# Revit family: LAMP_FLUT G2 ASYMMETRIC
name_source: partatom
category: Modelos genéricos
revit_build: Autodesk Revit 2015 (Build: 20140606_1530(x64)
units: mm (PartAtom-declared; Revit-internal decimal feet)

## types (12) — shared parameters
CRI = 70
Dimensions = 530 x 280 x 60
Elevación por defecto = 1219 mm
Fabricante = LAMP
Gear = Electronic
Installation instructions = https://www.lamp.es
Insulation class = I
Lamp = HIGH POWER LED
Last update = 22/08/2019
Luminaire type = OUTDOOR - FLOODLIGHT
MacAdam = 4
Manufacturer URL = http://www.lamp.es
Manufacturer country = Spain
Manufacturer name = LAMP
Material Rótula = LAMP_Acero inoxidable AISI 304
Material cuerpo = LAMP_Aluminio Cuerpo Flut ANT
Model explanation = Availability of tilting between 0º and -30º (or 120º) when placed in a project.
Power Supply = 220-240V 50-60Hz
Product URL = https://www.lamp.es
Product datasheet = http://www.lamp.es
Protection rating = IP66 / IK06
Type = HIGH POWER PHILIPS

## per-type parameters (varying)
| type | Descripción | Efficacy | Finish | IEE | Initial color | Initial intensity | LED Lifetime | Modelo | Photometric web file | Plum | Power | Product code | Weight |
| 7329LM 3000 ANTHRACITE | FLUT G2 9300 WW ASYM ANT. | 114 lm/W | Textured anthracite grey | A+ | 3000 K | 7329 lm | 50.000 L90 B10 | FL209AS730NA | Cuerpo Flut G2 - Asym : 7329LM 3000 ANTHRACITE | 64 W | 59 W | FL209AS730NA | 7.86 kg |
| 7329LM 3000 GREY | FLUT G2 9300 WW ASYM GR. | 114 lm/W | Texturised grey | A+ | 3000 K | 7329 lm | 50.000 L90 B10 | FL209AS730NG | Cuerpo Flut G2 - Asym : 7329LM 3000 GREY | 64 W | 59 W | FL209AS730NG | 7.86 kg |
| 7715LM 4000 ANTHRACITE | FLUT G2 9300 NW ASYM ANT. | 120 lm/W | Textured anthracite grey | A++ | 4000 K | 7715 lm | 50.000 L90 B10 | FL209AS740NA | Cuerpo Flut G2 - Asym : 7715LM 4000 ANTHRACITE | 64 W | 59 W | FL209AS740NA | 7.86 kg |
| 7715LM 4000 GREY | FLUT G2 9300 NW ASYM GR. | 120 lm/W | Texturised grey | A++ | 4000 K | 7715 lm | 50.000 L90 B10 | FL209AS740NG | Cuerpo Flut G2 - Asym : 7715LM 4000 GREY | 64 W | 59 W | FL209AS740NG | 7.86 kg |
| 11068LM 3000 ANTHRACITE | FLUT G2 14000 WW ASYM ANT. | 114 lm/W | Textured anthracite grey | A+ | 3000 K | 11068 lm | 80.000 L80 B10 | FL214AS730NA | Cuerpo Flut G2 - Asym : 11068LM 3000 ANTHRACITE | 97 W | 88 W | FL214AS730NA | 7.94 kg |
| 11068LM 3000 GREY | FLUT G2 14000 WW ASYM GR. | 114 lm/W | Texturised grey | A+ | 3000 K | 11068 lm | 80.000 L80 B10 | FL214AS730NG | Cuerpo Flut G2 - Asym : 11068LM 3000 GREY | 97 W | 88 W | FL214AS730NG | 7.94 kg |
| 11650LM 4000 ANTHRACITE | FLUT G2 14000 NW ASYM ANT. | 120 lm/W | Textured anthracite grey | A++ | 4000 K | 11650 lm | 80.000 L80 B10 | FL214AS740NA | Cuerpo Flut G2 - Asym : 11650LM 4000 ANTHRACITE | 97 W | 88 W | FL214AS740NA | 7.94 kg |
| 11650LM 4000 GREY | FLUT G2 14000 NW ASYM GR. | 120 lm/W | Texturised grey | A++ | 4000 K | 11650 lm | 80.000 L80 B10 | FL214AS740NG | Cuerpo Flut G2 - Asym : 11650LM 4000 GREY | 97 W | 88 W | FL214AS740NG | 7.94 kg |
| 14546LM 3000 ANTHRACITE | FLUT G2 18700 WW ASYM ANT. | 116 lm/W | Textured anthracite grey | A+ | 3000 K | 14546 lm | 75.000 L80 B10 | FL219AS730NA | Cuerpo Flut G2 - Asym : 14546LM 3000 ANTHRACITE | 125 W | 117 W | FL219AS730NA | 8.09 kg |
| 14546LM 3000 GREY | FLUT G2 18700 WW ASYM GR. | 116 lm/W | Texturised grey | A+ | 3000 K | 14546 lm | 75.000 L80 B10 | FL219AS730NG | Cuerpo Flut G2 - Asym : 14546LM 3000 GREY | 125 W | 117 W | FL219AS730NG | 8.09 kg |
| 15312LM 4000 ANTHRACITE | FLUT G2 18700 NW ASYM ANT. | 122 lm/W | Textured anthracite grey | A++ | 4000 K | 15312 lm | 75.000 L80 B10 | FL219AS740NA | Cuerpo Flut G2 - Asym : 15312LM 4000 ANTHRACITE | 125 W | 117 W | FL219AS740NA | 8.09 kg |
| 15312LM 4000 GREY | FLUT G2 18700 NW ASYM GR. | 122 lm/W | Texturised grey | A++ | 4000 K | 15312 lm | 75.000 L80 B10 | FL219AS740NG | Cuerpo Flut G2 - Asym : 15312LM 4000 GREY | 125 W | 117 W | FL219AS740NG | 8.09 kg |
